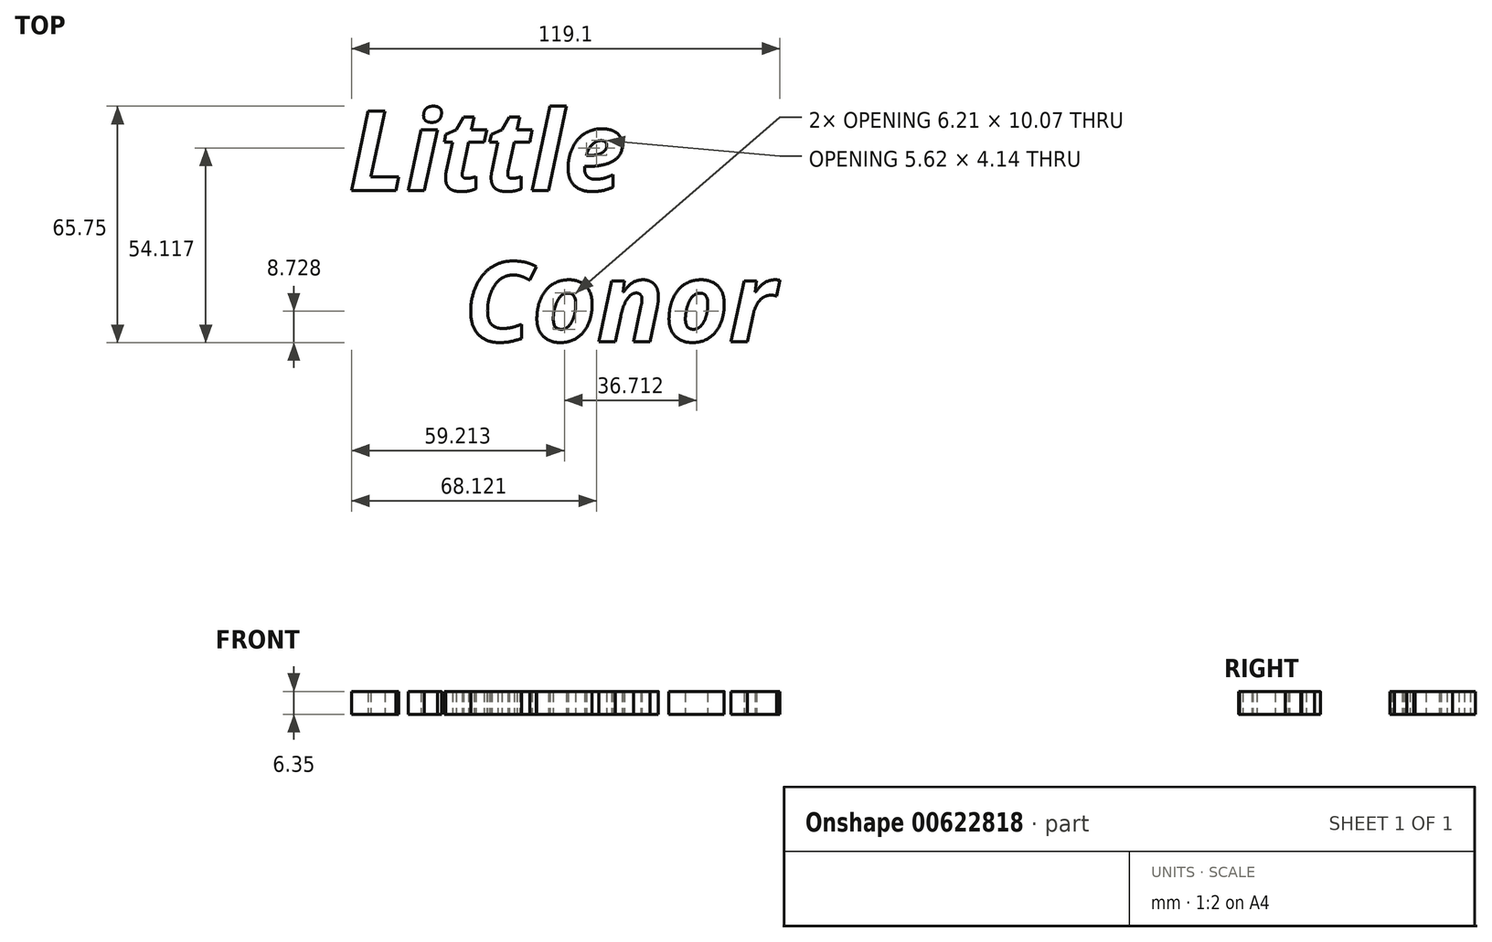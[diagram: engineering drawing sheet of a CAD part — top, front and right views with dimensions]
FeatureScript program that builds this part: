
annotation { "Feature Type Name" : "Feature", "Feature Type Description" : "" }
export const myFeature = defineFeature(function(context is Context, id is Id, definition is map)
    precondition{}
    {
        {
            var Q0;
            Q0=qCreatedBy(makeId("Top.planeOp"),FACE);
            var sketch = newSketch(context, id + "F0", { "sketchPlane" : qUnion([Q0])});
            skText(sketch, "E0", { "text": "Little \n    Conor", "fontName": "OpenSans-BoldItalic.ttf"});
            const initialGuessF0  = {"E0": [-0.0003, 6e-05, 1, 0, 0.02223]};
            skSetInitialGuess(sketch, initialGuessF0);
            skSolve(sketch);
        }
        {
            var Q0;
            Q0 = qSketchRegion(id + "F0", true);
            extrude(context, id + "F1", {"entities" : qUnion([Q0]), "depth" : 6.35 * mm, "offsetDistance" : 25.4 * mm});
        }
    });
